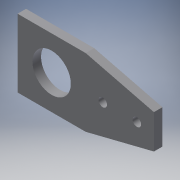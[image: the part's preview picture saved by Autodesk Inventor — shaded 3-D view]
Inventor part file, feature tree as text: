
AUTODESK INVENTOR PART (.ipt)
format: ipt  version: 2016 (Build 200138000, 138)  size: 108,544 bytes
history: native  units: in
note: dims shown in document units (in); Inventor stores cm internally (conversion verified against a paired STEP export)
features: extrude x1, sketch x1
ambient origin geometry x8: Origin, YZ Plane, XZ Plane, XY Plane, X Axis, Y Axis, Z Axis, Center Point
bodies: Solid1 (feature_tree)
feature tree (2):
  extrude  "Extrusion1"  Depth=2.0in
  sketch  "Sketch1"  dims[d1=2.0in d2=2.0in d3=2.0in d4=1.0in d5=1.125in d6=1.0in d7=1.0in d8=0.25in d9=0.25in d10=0.5in d11=1.0in d12=0.25in d13=0.0in]
